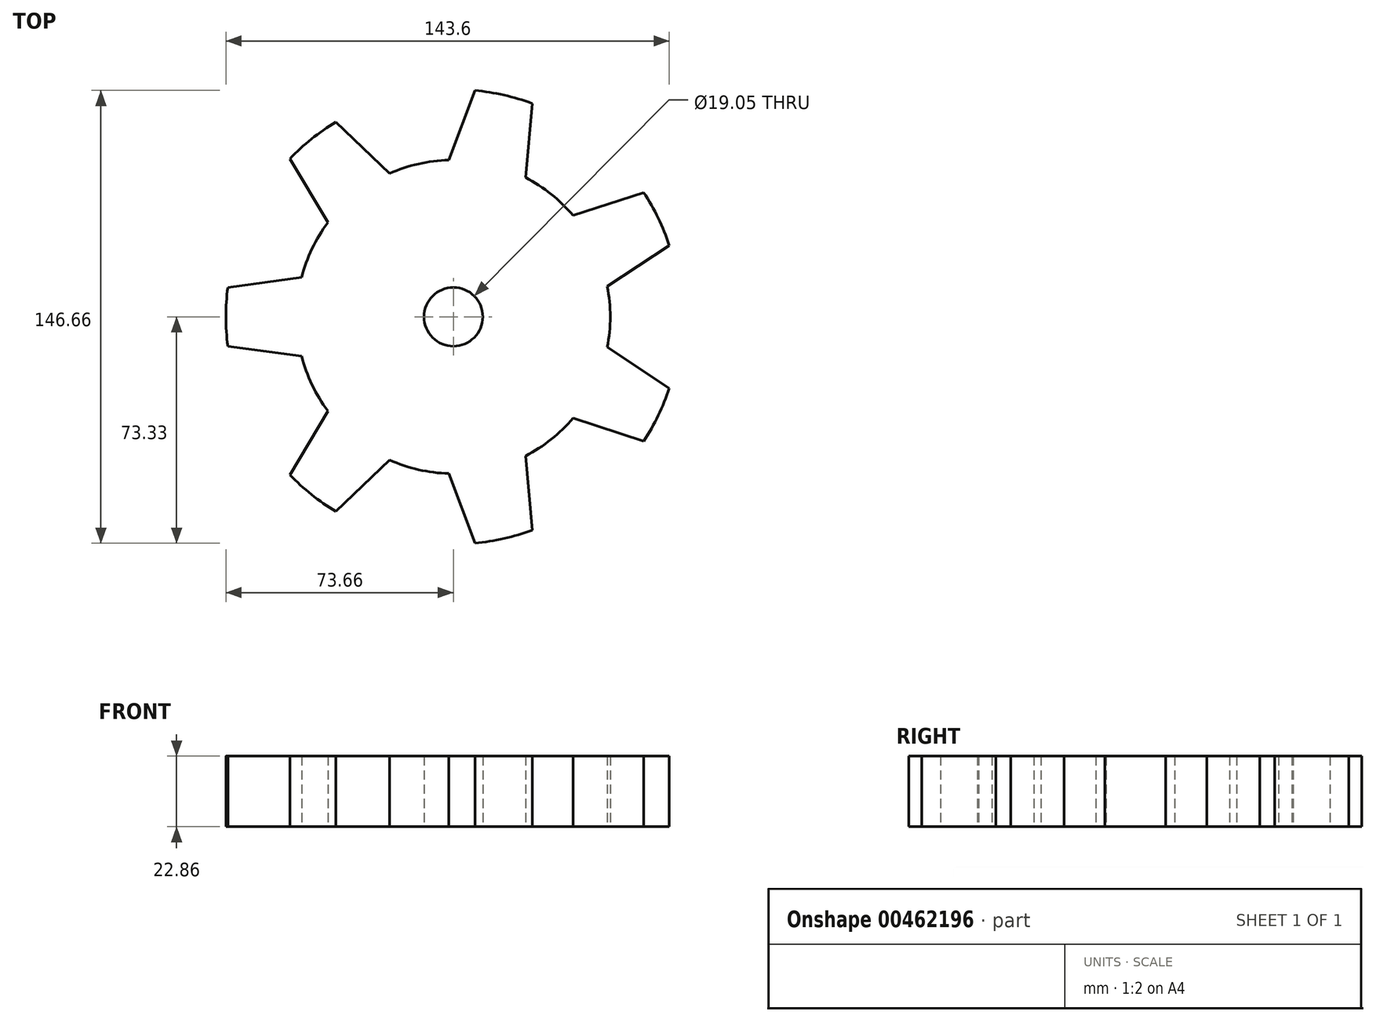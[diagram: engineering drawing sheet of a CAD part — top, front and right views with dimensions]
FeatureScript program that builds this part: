
annotation { "Feature Type Name" : "Feature", "Feature Type Description" : "" }
export const myFeature = defineFeature(function(context is Context, id is Id, definition is map)
    precondition{}
    {
        {
            var Q0;
            Q0=qCreatedBy(makeId("Top.planeOp"),FACE);
            var sketch = newSketch(context, id + "F0", { "sketchPlane" : qUnion([Q0])});
            skCircle(sketch, "E0", {"center": v(0, 0) * mm, "radius": 50.8 * mm});
            skLineSegment(sketch, "E1", {"start": v(0, 0) * mm, "end": v(-91.39, 0) * mm, "construction": true});
            skLineSegment(sketch, "E2", {"start": v(-73.04, 9.53) * mm, "end": v(-45.72, 13.2) * mm});
            skLineSegment(sketch, "E3", {"start": v(-45.72, 13.2) * mm, "end": v(-45.72, 0) * mm});
            skLineSegment(sketch, "E4.MirrorCS", {"start": v(-45.72, -13.2) * mm, "end": v(-45.72, 0) * mm});
            skLineSegment(sketch, "E5.MirrorCS", {"start": v(-73.04, -9.53) * mm, "end": v(-45.72, -13.2) * mm});
            skArc(sketch, "E6", {"start": v(-73.04, 9.52) * mm, "mid": v(-73.66, 0) * mm, "end": v(-73.04, -9.53) * mm});
            skPoint(sketch, "E7.end.orphan", {"position": v(-74.04, 9.39) * mm});
            skPoint(sketch, "E7.start.orphan", {"position": v(-73.66, 0) * mm});
            skPoint(sketch, "E8.MirrorCS.end.orphan", {"position": v(-74.04, -9.39) * mm});
            skLineSegment(sketch, "E9.1.0", {"start": v(-52.99, -51.17) * mm, "end": v(-38.83, -27.51) * mm});
            skLineSegment(sketch, "E9.1.1", {"start": v(-38.83, -27.51) * mm, "end": v(-28.5, -35.75) * mm});
            skLineSegment(sketch, "E9.1.2", {"start": v(-18.18, -43.98) * mm, "end": v(-28.5, -35.75) * mm});
            skLineSegment(sketch, "E9.1.3", {"start": v(-38.1, -63.04) * mm, "end": v(-18.18, -43.98) * mm});
            skArc(sketch, "E9.1.4", {"start": v(-52.99, -51.17) * mm, "mid": v(-45.93, -57.59) * mm, "end": v(-38.1, -63.04) * mm});
            skLineSegment(sketch, "E9.2.0", {"start": v(6.97, -73.33) * mm, "end": v(-2.7, -47.51) * mm});
            skLineSegment(sketch, "E9.2.1", {"start": v(-2.7, -47.51) * mm, "end": v(10.17, -44.57) * mm});
            skLineSegment(sketch, "E9.2.2", {"start": v(23.05, -41.63) * mm, "end": v(10.17, -44.57) * mm});
            skLineSegment(sketch, "E9.2.3", {"start": v(25.54, -69.1) * mm, "end": v(23.05, -41.63) * mm});
            skArc(sketch, "E9.2.4", {"start": v(6.97, -73.33) * mm, "mid": v(16.4, -71.81) * mm, "end": v(25.54, -69.1) * mm});
            skLineSegment(sketch, "E9.3.0", {"start": v(61.68, -40.27) * mm, "end": v(35.46, -31.74) * mm});
            skLineSegment(sketch, "E9.3.1", {"start": v(35.46, -31.74) * mm, "end": v(41.2, -19.84) * mm});
            skLineSegment(sketch, "E9.3.2", {"start": v(46.92, -7.94) * mm, "end": v(41.2, -19.84) * mm});
            skLineSegment(sketch, "E9.3.3", {"start": v(69.94, -23.1) * mm, "end": v(46.92, -7.94) * mm});
            skArc(sketch, "E9.3.4", {"start": v(61.68, -40.27) * mm, "mid": v(66.37, -31.96) * mm, "end": v(69.94, -23.1) * mm});
            skLineSegment(sketch, "E9.4.0", {"start": v(69.94, 23.1) * mm, "end": v(46.92, 7.94) * mm});
            skLineSegment(sketch, "E9.4.1", {"start": v(46.92, 7.94) * mm, "end": v(41.2, 19.84) * mm});
            skLineSegment(sketch, "E9.4.2", {"start": v(35.46, 31.74) * mm, "end": v(41.2, 19.84) * mm});
            skLineSegment(sketch, "E9.4.3", {"start": v(61.68, 40.27) * mm, "end": v(35.46, 31.74) * mm});
            skArc(sketch, "E9.4.4", {"start": v(69.94, 23.1) * mm, "mid": v(66.37, 31.96) * mm, "end": v(61.68, 40.27) * mm});
            skLineSegment(sketch, "E9.5.0", {"start": v(25.54, 69.1) * mm, "end": v(23.05, 41.63) * mm});
            skLineSegment(sketch, "E9.5.1", {"start": v(23.05, 41.63) * mm, "end": v(10.17, 44.57) * mm});
            skLineSegment(sketch, "E9.5.2", {"start": v(-2.7, 47.51) * mm, "end": v(10.17, 44.57) * mm});
            skLineSegment(sketch, "E9.5.3", {"start": v(6.97, 73.33) * mm, "end": v(-2.7, 47.51) * mm});
            skArc(sketch, "E9.5.4", {"start": v(25.54, 69.1) * mm, "mid": v(16.4, 71.81) * mm, "end": v(6.97, 73.33) * mm});
            skLineSegment(sketch, "E9.6.0", {"start": v(-38.1, 63.04) * mm, "end": v(-18.18, 43.98) * mm});
            skLineSegment(sketch, "E9.6.1", {"start": v(-18.18, 43.98) * mm, "end": v(-28.5, 35.75) * mm});
            skLineSegment(sketch, "E9.6.2", {"start": v(-38.83, 27.51) * mm, "end": v(-28.5, 35.75) * mm});
            skLineSegment(sketch, "E9.6.3", {"start": v(-52.99, 51.17) * mm, "end": v(-38.83, 27.51) * mm});
            skArc(sketch, "E9.6.4", {"start": v(-38.1, 63.04) * mm, "mid": v(-45.93, 57.59) * mm, "end": v(-52.99, 51.17) * mm});
            skCircle(sketch, "E10", {"center": v(0, 0) * mm, "radius": 9.53 * mm});
            skSolve(sketch);
        }
        {
            var Q0;
            {var subQ5=sQuery(id+"F0.wireOp",EDGE,"E9.6.4");Q0=makeQuery(id+"F0.imprint","IMPRINT",FACE,{"disambiguationData":[TD([[makeQuery(id+"F0.imprint","IMPRINT",EDGE,{"derivedFrom":subQ5}),1.0]])]});}
            var Q1;
            {var subQ0=sQuery(id+"F0.wireOp",EDGE,"E9.6.1");Q1=makeQuery(id+"F0.imprint","IMPRINT",FACE,{"disambiguationData":[TD([[makeQuery(id+"F0.imprint","IMPRINT",EDGE,{"derivedFrom":subQ0}),-1.0]])]});}
            var Q2;
            {var subQ21=sQuery(id+"F0.wireOp",EDGE,"E3");Q2=makeQuery(id+"F0.imprint","IMPRINT",FACE,{"disambiguationData":[TD([[makeQuery(id+"F0.imprint","IMPRINT",EDGE,{"derivedFrom":subQ21}),1.0]])]});}
            var Q3;
            {var subQ5=sQuery(id+"F0.wireOp",EDGE,"E9.5.4");Q3=makeQuery(id+"F0.imprint","IMPRINT",FACE,{"disambiguationData":[TD([[makeQuery(id+"F0.imprint","IMPRINT",EDGE,{"derivedFrom":subQ5}),1.0]])]});}
            var Q4;
            {var subQ0=sQuery(id+"F0.wireOp",EDGE,"E9.4.1");Q4=makeQuery(id+"F0.imprint","IMPRINT",FACE,{"disambiguationData":[TD([[makeQuery(id+"F0.imprint","IMPRINT",EDGE,{"derivedFrom":subQ0}),-1.0]])]});}
            var Q5;
            {var subQ5=sQuery(id+"F0.wireOp",EDGE,"E9.4.4");Q5=makeQuery(id+"F0.imprint","IMPRINT",FACE,{"disambiguationData":[TD([[makeQuery(id+"F0.imprint","IMPRINT",EDGE,{"derivedFrom":subQ5}),1.0]])]});}
            var Q6;
            {var subQ0=sQuery(id+"F0.wireOp",EDGE,"E9.5.1");Q6=makeQuery(id+"F0.imprint","IMPRINT",FACE,{"disambiguationData":[TD([[makeQuery(id+"F0.imprint","IMPRINT",EDGE,{"derivedFrom":subQ0}),-1.0]])]});}
            var Q7;
            {var subQ1=sQuery(id+"F0.wireOp",EDGE,"E9.3.1");Q7=makeQuery(id+"F0.imprint","IMPRINT",FACE,{"disambiguationData":[TD([[makeQuery(id+"F0.imprint","IMPRINT",EDGE,{"derivedFrom":subQ1}),-1.0]])]});}
            var Q8;
            {var subQ5=sQuery(id+"F0.wireOp",EDGE,"E9.3.4");Q8=makeQuery(id+"F0.imprint","IMPRINT",FACE,{"disambiguationData":[TD([[makeQuery(id+"F0.imprint","IMPRINT",EDGE,{"derivedFrom":subQ5}),1.0]])]});}
            var Q9;
            {var subQ1=sQuery(id+"F0.wireOp",EDGE,"E9.2.1");Q9=makeQuery(id+"F0.imprint","IMPRINT",FACE,{"disambiguationData":[TD([[makeQuery(id+"F0.imprint","IMPRINT",EDGE,{"derivedFrom":subQ1}),-1.0]])]});}
            var Q10;
            {var subQ5=sQuery(id+"F0.wireOp",EDGE,"E9.2.4");Q10=makeQuery(id+"F0.imprint","IMPRINT",FACE,{"disambiguationData":[TD([[makeQuery(id+"F0.imprint","IMPRINT",EDGE,{"derivedFrom":subQ5}),1.0]])]});}
            var Q11;
            {var subQ1=sQuery(id+"F0.wireOp",EDGE,"E9.1.1");Q11=makeQuery(id+"F0.imprint","IMPRINT",FACE,{"disambiguationData":[TD([[makeQuery(id+"F0.imprint","IMPRINT",EDGE,{"derivedFrom":subQ1}),-1.0]])]});}
            var Q12;
            {var subQ5=sQuery(id+"F0.wireOp",EDGE,"E9.1.4");Q12=makeQuery(id+"F0.imprint","IMPRINT",FACE,{"disambiguationData":[TD([[makeQuery(id+"F0.imprint","IMPRINT",EDGE,{"derivedFrom":subQ5}),1.0]])]});}
            var Q13;
            {var subQ6=sQuery(id+"F0.wireOp",EDGE,"E3");Q13=makeQuery(id+"F0.imprint","IMPRINT",FACE,{"disambiguationData":[TD([[makeQuery(id+"F0.imprint","IMPRINT",EDGE,{"derivedFrom":subQ6}),-1.0]])]});}
            var Q14;
            {var subQ5=sQuery(id+"F0.wireOp",EDGE,"E6");Q14=makeQuery(id+"F0.imprint","IMPRINT",FACE,{"disambiguationData":[TD([[makeQuery(id+"F0.imprint","IMPRINT",EDGE,{"derivedFrom":subQ5}),1.0]])]});}
            extrude(context, id + "F1", {"entities" : qUnion([Q0, Q1, Q2, Q3, Q4, Q5, Q6, Q7, Q8, Q9, Q10, Q11, Q12, Q13, Q14]), "depth" : 22.86 * mm});
        }
    });
